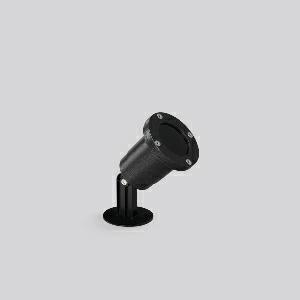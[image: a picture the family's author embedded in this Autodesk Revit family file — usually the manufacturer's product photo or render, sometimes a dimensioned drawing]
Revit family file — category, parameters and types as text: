
# Revit family: par16_722221_0031_c43d
name_source: partatom
category: Lighting Fixtures
units: mm (PartAtom-declared; Revit-internal decimal feet)

## family parameters
Cut with Voids When Loaded = No
Host = Face
Light Source = No
Part Type = Normal
Room Calculation Point = No
Round Connector Dimension = Use Diameter
Shared = No

## types (1)
- PAR16 (1 x LED Modul 830, 140 lm, 3000)
    Apparent Load = 4 VA
    CIE Flux Codes = 52 84 98 100 100
    Color Rendering = 80
    Color Temperature = 3000
    Default Elevation = 1800 mm
    Description = Series: PAR16
Garden spotlight with earth spike. Housing: die-cast aluminium, powder-coated. Safety glass, clear. Peg made of fiber reinforced plastic. Exchangeable mains voltage LED. With 3 m connection cable including safety plug (Schuko). 
Colour: anthracite metallic (DB703)
Length: 157 mm
Width: 98 mm
Height: 275 mm
Lamp: LED
System power: 4.4 W
Rated luminous flux: 140 lm
Luminous efficiency: 32 lm/W
Control gear: Converter not necessary
Protection class: I
Type of protection: IP 55
    Height = 275 mm
    Lamp = 1 x LED Modul 830
    Lamp Light Flux = 140 lm
    Lamp count = 1
    Length = 157 mm
    Lifetime = 50000 h
    Luminous efficacy = 32 lm/W
    Manufacturer = RZB
    ModVariant = No
    Model = 722221.0031
    Mounting Place = Floor
    Mounting Type = Freestanding
    Number of Poles = 1
    OnlyDefault = Yes
    Power Factor = 1
    Product Name = PAR16
    Product group = Floodlights and spotlights
    ProductGroupID = 1354
    Protection Class = Protection class I
    Protection Degree = IP 55
    RLX_Detail_Level = 1
    RLX_Emergency_Light_Flux = 0 lm
    RLX_Emergency_Type = 0
    RLX_Emergency_Type_DB = No
    RlxData = <blob elided: 38553 chars, md5=b47d7c9f>
    Socket = socket
    Standby Power = 0 W
    System Light Flux = 140 lm
    System Power = 4 W
    Type Comments = Product without accessories
    Type Image = 721680.0031.jpg
    URL = http://relux.com
    VarID = ---
    Voltage = 0 V
    Weight = 0.00 kg
    Width = 98 mm

## geometry (parser evidence)
native form markers: Blend x4, Sweep x10
no freeform markers — native parametric forms only
